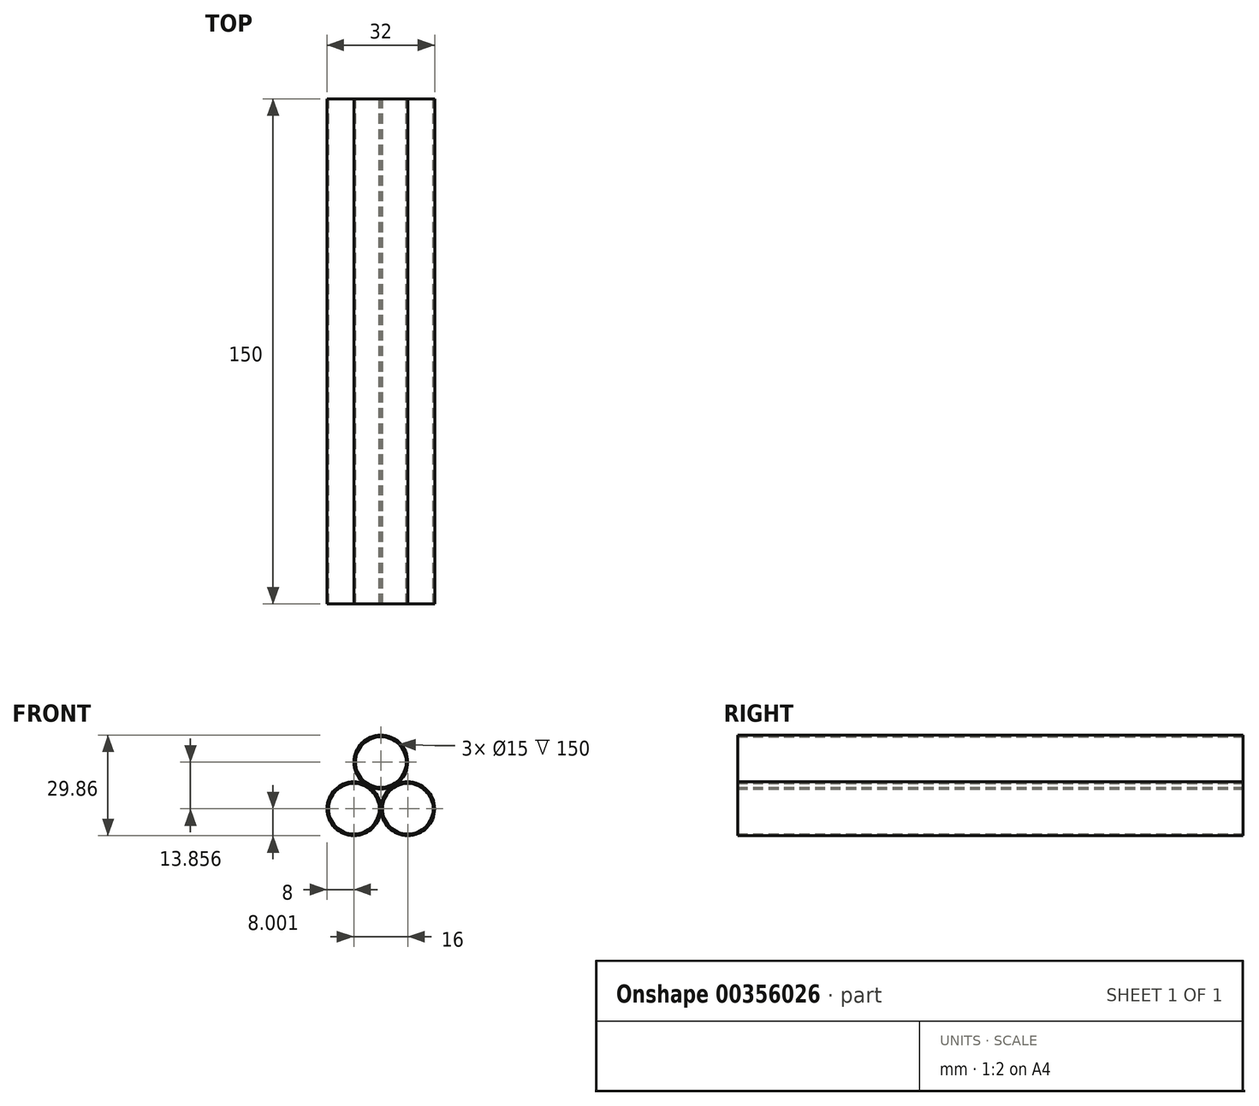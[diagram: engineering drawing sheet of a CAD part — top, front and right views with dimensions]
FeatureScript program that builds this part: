
annotation { "Feature Type Name" : "Feature", "Feature Type Description" : "" }
export const myFeature = defineFeature(function(context is Context, id is Id, definition is map)
    precondition{}
    {
        {
            var Q0;
            Q0=qCreatedBy(makeId("Front.planeOp"),FACE);
            var sketch = newSketch(context, id + "F0", { "sketchPlane" : qUnion([Q0])});
            skCircle(sketch, "E0", {"center": v(0, 0) * mm, "radius": 17.24 * mm});
            skPoint(sketch, "E1", {"position": v(0, 9.24) * mm});
            skCircle(sketch, "E2", {"center": v(0, 9.24) * mm, "radius": 8 * mm});
            skCircle(sketch, "E3", {"center": v(0, 9.24) * mm, "radius": 7.5 * mm});
            skCircle(sketch, "E4", {"center": v(-123.59, 6.74) * mm, "radius": 13.4 * mm});
            skCircle(sketch, "E5.1.0", {"center": v(-8, -4.62) * mm, "radius": 7.5 * mm});
            skCircle(sketch, "E5.1.1", {"center": v(-8, -4.62) * mm, "radius": 8 * mm});
            skCircle(sketch, "E5.2.0", {"center": v(8, -4.62) * mm, "radius": 7.5 * mm});
            skCircle(sketch, "E5.2.1", {"center": v(8, -4.62) * mm, "radius": 8 * mm});
            skSolve(sketch);
        }
        {
            var Q0;
            Q0=makeQuery(id+"F0.imprint","IMPRINT",FACE,{"disambiguationData":[TD([[makeQuery(id+"F0.imprint","IMPRINT",EDGE,{"derivedFrom":sQuery(id+"F0.wireOp",EDGE,"E3")}),-1.0]])]});
            var Q1;
            Q1=makeQuery(id+"F0.imprint","IMPRINT",FACE,{"disambiguationData":[TD([[makeQuery(id+"F0.imprint","IMPRINT",EDGE,{"derivedFrom":sQuery(id+"F0.wireOp",EDGE,"E5.1.0")}),-1.0]])]});
            var Q2;
            Q2=makeQuery(id+"F0.imprint","IMPRINT",FACE,{"disambiguationData":[TD([[makeQuery(id+"F0.imprint","IMPRINT",EDGE,{"derivedFrom":sQuery(id+"F0.wireOp",EDGE,"E5.2.0")}),-1.0]])]});
            extrude(context, id + "F1", {"entities" : qUnion([Q0, Q1, Q2]), "depth" : 150 * mm});
        }
    });
